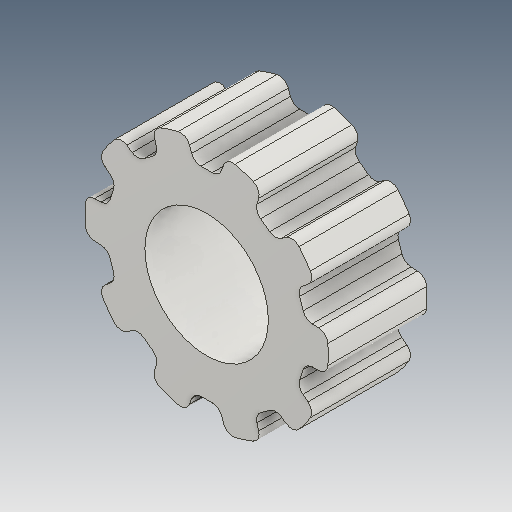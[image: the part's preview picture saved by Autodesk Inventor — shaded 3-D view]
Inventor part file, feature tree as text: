
AUTODESK INVENTOR PART (.ipt)
format: ipt  version: 2020.3 (Build 243373010, 373A)  size: 253,952 bytes
history: native  units: mm (DEFAULTED — no unit token found)
features: other x3, extrude x3, fillet x1, pattern_circular x1, sketch x1
ambient origin geometry x8: Origin, YZ Plane, XZ Plane, XY Plane, X Axis, Y Axis, Z Axis, Center Point
bodies: Solid1 (feature_tree)
feature tree (9):
  other  "Pulley Sketch"
  extrude  "Base Body"  Depth=1.1684mm
  extrude  "Tooth"  Depth=1.1684mm
  fillet  "Tooth Fillet"  Radius=6.981317mm
  pattern_circular  "Teeth"  [2 undecoded]
  other  "Left flange"
  other  "Right flange"
  extrude  "Extrusion3"  Depth=12.0mm
  sketch  "Sketch2"  dims[d0=30.319017mm d1=0.381mm d2=2.667mm d3=6.981317mm d4=3.048mm d5=12.0mm d6=0.0mm d7=12.0mm d8=0.0mm d9=1.1938mm d10=1.1684mm d11=100.0mm d12=360.0deg d15=0.0mm d16=0.0mm d17=15.0mm d18=0.0mm d19=0.0mm]
note: 2 required parameter values undecoded (feature->parameter linkage not recoverable at this tier; creation-order binding heuristic only, values carry confidence <= 0.55)
